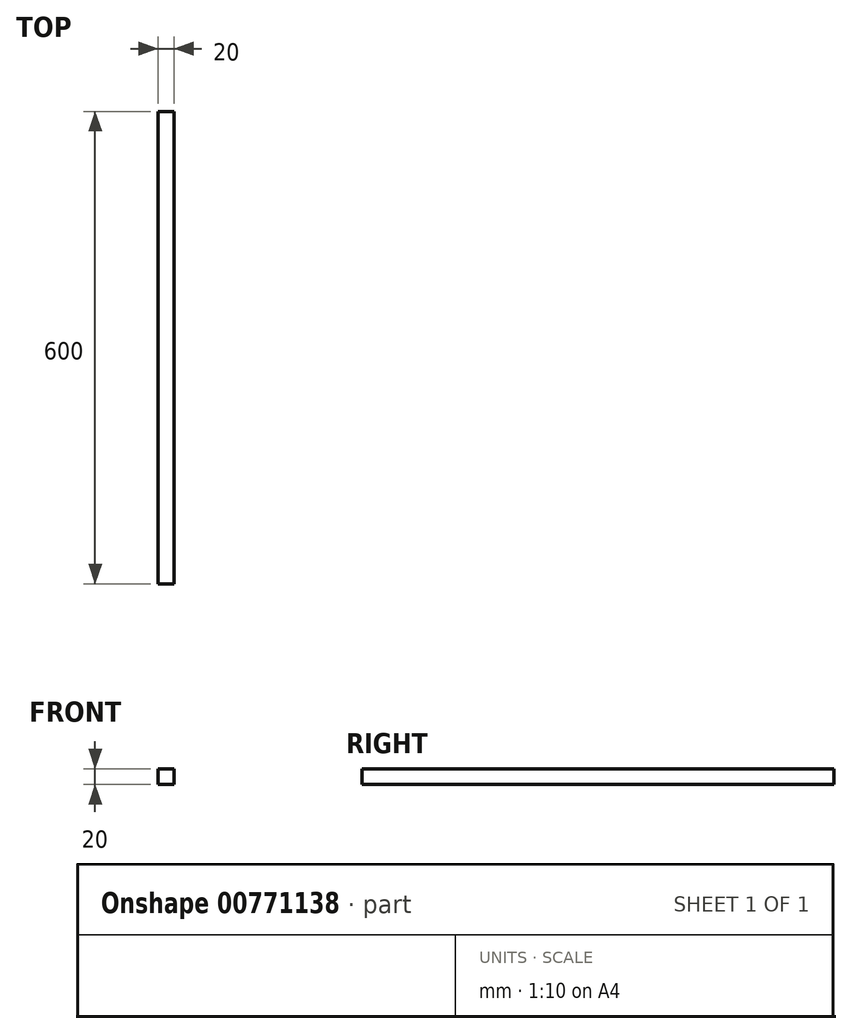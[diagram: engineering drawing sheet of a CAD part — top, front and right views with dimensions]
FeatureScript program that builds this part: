
annotation { "Feature Type Name" : "Feature", "Feature Type Description" : "" }
export const myFeature = defineFeature(function(context is Context, id is Id, definition is map)
    precondition{}
    {
        {
            var Q0;
            Q0=qCreatedBy(makeId("Front.planeOp"),FACE);
            var sketch = newSketch(context, id + "F0", { "sketchPlane" : qUnion([Q0])});
            skLineSegment(sketch, "E0.bottom", {"start": v(10, -10) * mm, "end": v(-10, -10) * mm});
            skLineSegment(sketch, "E0.top", {"start": v(10, 10) * mm, "end": v(-10, 10) * mm});
            skLineSegment(sketch, "E0.left", {"start": v(10, -10) * mm, "end": v(10, 10) * mm});
            skLineSegment(sketch, "E0.right", {"start": v(-10, -10) * mm, "end": v(-10, 10) * mm});
            skPoint(sketch, "E0.middle", {"position": v(0, 0) * mm});
            skSolve(sketch);
        }
        {
            var Q0;
            Q0 = qSketchRegion(id + "F0", true);
            extrude(context, id + "F1", {"entities" : qUnion([Q0]), "depth" : 600 * mm, "offsetDistance" : 25 * mm});
        }
    });
